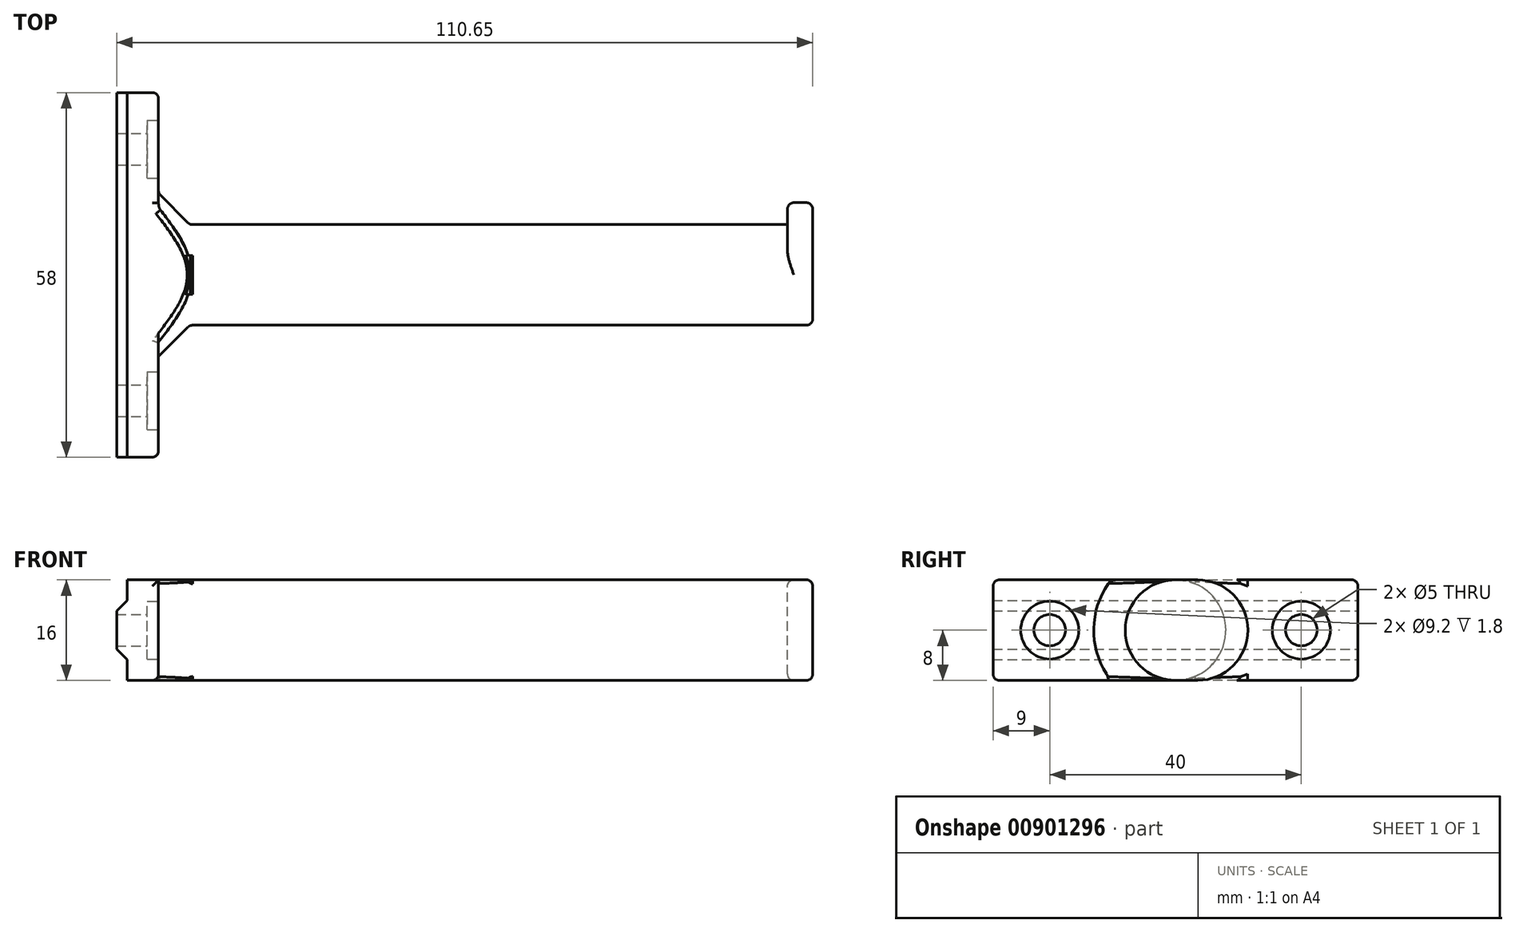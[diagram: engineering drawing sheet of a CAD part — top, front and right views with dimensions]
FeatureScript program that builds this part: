
annotation { "Feature Type Name" : "Feature", "Feature Type Description" : "" }
export const myFeature = defineFeature(function(context is Context, id is Id, definition is map)
    precondition{}
    {
        {
            var Q0;
            Q0=qCreatedBy(makeId("Right.planeOp"),FACE);
            var sketch = newSketch(context, id + "F0", { "sketchPlane" : qUnion([Q0])});
            skCircle(sketch, "E0", {"center": v(0, 0) * mm, "radius": 8 * mm});
            skSolve(sketch);
        }
        {
            var Q0;
            Q0=qSketchRegion(id+"F0",true);
            extrude(context, id + "F1", {"entities" : qUnion([Q0]), "depth" : 95 * mm});
        }
        {
            var Q0;
            Q0=makeQuery(id+"F1.opExtrude","CAP_FACE",FACE,{"disambiguationData":[OSD([sQuery(id+"F0.wireOp",EDGE,"E0")])],"isStart":false});
            var sketch = newSketch(context, id + "F2", { "sketchPlane" : qUnion([Q0])});
            skArc(sketch, "E1", {"start": v(1.75, 7.8) * mm, "mid": v(-8, 0) * mm, "end": v(1.75, -7.8) * mm});
            skLineSegment(sketch, "E2", {"start": v(0, 0) * mm, "end": v(30.67, 0) * mm, "construction": true});
            skArc(sketch, "E3", {"start": v(3.5, -8) * mm, "mid": v(11.5, 0) * mm, "end": v(3.5, 8) * mm});
            skLineSegment(sketch, "E4", {"start": v(3.5, 8) * mm, "end": v(0, 8) * mm});
            skLineSegment(sketch, "E5", {"start": v(3.5, -8) * mm, "end": v(0, -8) * mm});
            skSolve(sketch);
        }
        {
            var Q0;
            Q0=qSketchRegion(id+"F2",true);
            extrude(context, id + "F3", {"entities" : qUnion([Q0]), "operationType" : NewBodyOperationType.ADD, "depth" : 4 * mm});
        }
        {
            var Q0;
            Q0=qCreatedBy(makeId("Top.planeOp"),FACE);
            var sketch = newSketch(context, id + "F4", { "sketchPlane" : qUnion([Q0])});
            skLineSegment(sketch, "E6", {"start": v(0, 0) * mm, "end": v(0, 8) * mm});
            skLineSegment(sketch, "E7", {"start": v(0, 8) * mm, "end": v(-5, 13) * mm});
            skLineSegment(sketch, "E8", {"start": v(-5, 13) * mm, "end": v(-5, 0) * mm});
            skLineSegment(sketch, "E9", {"start": v(26.22, 0) * mm, "end": v(-29.93, 0) * mm, "construction": true});
            skLineSegment(sketch, "E10", {"start": v(0, 0) * mm, "end": v(-5, 0) * mm});
            skSolve(sketch);
        }
        {
            var Q0;
            Q0=qSketchRegion(id+"F4",true);
            var Q1;
            Q1=sQuery(id+"F4.wireOp",EDGE,"E9");
            revolve(context, id + "F5", {"operationType" : NewBodyOperationType.ADD, "entities" : qUnion([Q0]), "axis" : qUnion([Q1]), "revolveType" : RevolveType.FULL});
        }
        {
            var Q0;
            Q0=makeQuery(id+"F5.opRevolve","SWEPT_FACE",FACE,{"disambiguationData":[OSD([sQuery(id+"F4.wireOp",EDGE,"E8")])]});
            var sketch = newSketch(context, id + "F6", { "sketchPlane" : qUnion([Q0])});
            skLineSegment(sketch, "E11", {"start": v(0, 0) * mm, "end": v(-25.76, 0) * mm, "construction": true});
            skLineSegment(sketch, "E12.bottom", {"start": v(-29, -8) * mm, "end": v(29, -8) * mm});
            skLineSegment(sketch, "E12.top", {"start": v(-29, 8) * mm, "end": v(29, 8) * mm});
            skLineSegment(sketch, "E12.left", {"start": v(-29, -8) * mm, "end": v(-29, 8) * mm});
            skLineSegment(sketch, "E12.right", {"start": v(29, -8) * mm, "end": v(29, 8) * mm});
            skPoint(sketch, "E12.middle", {"position": v(0, 0) * mm});
            skPoint(sketch, "E13", {"position": v(-20, 0) * mm});
            skPoint(sketch, "E14.MirrorP", {"position": v(20, 0) * mm});
            skSolve(sketch);
        }
        {
            var Q0;
            Q0=qSketchRegion(id+"F6",true);
            extrude(context, id + "F7", {"entities" : qUnion([Q0]), "operationType" : NewBodyOperationType.ADD, "depth" : 5 * mm});
        }
        {
            var Q0;
            {var subQ0=sQuery(id+"F6.wireOp",EDGE,"E12.bottom");var subQ1=makeQuery(id+"F5.opRevolve","SWEPT_EDGE",EDGE,{"disambiguationData":[OSD([sQuery(id+"F4.wireOp",EDGE,"E7"),sQuery(id+"F4.wireOp",EDGE,"E8")])]});var subQ2=makeQuery(id+"F6.imprint","INTERSECT",VERTEX,{"disambiguationData":[OD(0.0)],"derivedFrom":[subQ1,subQ0]});Q0=makeQuery(id+"F6.imprint","IMPRINT",FACE,{"disambiguationData":[TD([[makeQuery(id+"F6.imprint","IMPRINT",EDGE,{"disambiguationData":[TD([[subQ2,-1.0]])],"derivedFrom":subQ0}),-1.0]])]});}
            var sketch = newSketch(context, id + "F8", { "sketchPlane" : qUnion([Q0])});
            skLineSegment(sketch, "E15.bottom", {"start": v(-35.92, -15.92) * mm, "end": v(35.92, -15.92) * mm});
            skLineSegment(sketch, "E15.top", {"start": v(-35.92, 15.92) * mm, "end": v(35.92, 15.92) * mm});
            skLineSegment(sketch, "E15.left", {"start": v(-35.92, -15.92) * mm, "end": v(-35.92, 15.92) * mm});
            skLineSegment(sketch, "E15.right", {"start": v(35.92, -15.92) * mm, "end": v(35.92, 15.92) * mm});
            skPoint(sketch, "E15.middle", {"position": v(0, 0) * mm});
            skLineSegment(sketch, "E16.bottom", {"start": v(-29, -8) * mm, "end": v(29, -8) * mm});
            skLineSegment(sketch, "E16.top", {"start": v(-29, 8) * mm, "end": v(29, 8) * mm});
            skLineSegment(sketch, "E16.left", {"start": v(-29, -8) * mm, "end": v(-29, 8) * mm});
            skLineSegment(sketch, "E16.right", {"start": v(29, -8) * mm, "end": v(29, 8) * mm});
            skSolve(sketch);
        }
        {
            var Q0;
            Q0=qSketchRegion(id+"F8",true);
            extrude(context, id + "F9", {"entities" : qUnion([Q0]), "operationType" : NewBodyOperationType.REMOVE, "endBound" : BoundingType.THROUGH_ALL, "oppositeDirection" : true, "depth" : 25 * mm});
        }
        {
            var Q0;
            Q0=makeQuery(id+"F9.boolean.opBoolean","SPLIT",EDGE,{"disambiguationData":[OD(0.0)],"derivedFrom":makeQuery(id+"F5.boolean.opBoolean","MERGE",EDGE,{"derivedFrom":[makeQuery(id+"F1.opExtrude","CAP_EDGE",EDGE,{"disambiguationData":[OSD([sQuery(id+"F0.wireOp",EDGE,"E0")])],"isStart":true}),makeQuery(id+"F5.opRevolve","SWEPT_EDGE",EDGE,{"disambiguationData":[OSD([sQuery(id+"F4.wireOp",EDGE,"E6"),sQuery(id+"F4.wireOp",EDGE,"E7")])]})]})});
            var Q1;
            Q1=makeQuery(id+"F9.boolean.opBoolean","SPLIT",EDGE,{"disambiguationData":[OD(1.0)],"derivedFrom":makeQuery(id+"F5.boolean.opBoolean","MERGE",EDGE,{"derivedFrom":[makeQuery(id+"F1.opExtrude","CAP_EDGE",EDGE,{"disambiguationData":[OSD([sQuery(id+"F0.wireOp",EDGE,"E0")])],"isStart":true}),makeQuery(id+"F5.opRevolve","SWEPT_EDGE",EDGE,{"disambiguationData":[OSD([sQuery(id+"F4.wireOp",EDGE,"E6"),sQuery(id+"F4.wireOp",EDGE,"E7")])]})]})});
            var Q2;
            {var subQ0=sQuery(id+"F4.wireOp",EDGE,"E7");Q2=makeQuery(id+"F7.boolean.opBoolean","SPLIT",EDGE,{"disambiguationData":[topologyDisambiguationEdgeConnected([makeQuery(id+"F5.opRevolve","SWEPT_FACE",FACE,{"disambiguationData":[OSD([subQ0])]}),makeQuery(id+"F7.opExtrude","CAP_FACE",FACE,{"disambiguationData":[OSD([sQuery(id+"F6.wireOp",EDGE,"E12.bottom"),sQuery(id+"F6.wireOp",EDGE,"E12.top"),sQuery(id+"F6.wireOp",EDGE,"E12.left"),sQuery(id+"F6.wireOp",EDGE,"E12.right")])],"isStart":true})]),OD(0.0)],"derivedFrom":makeQuery(id+"F5.opRevolve","SWEPT_EDGE",EDGE,{"disambiguationData":[OSD([subQ0,sQuery(id+"F4.wireOp",EDGE,"E8")])]})});}
            var Q3;
            {var subQ0=sQuery(id+"F4.wireOp",EDGE,"E7");Q3=makeQuery(id+"F7.boolean.opBoolean","SPLIT",EDGE,{"disambiguationData":[topologyDisambiguationEdgeConnected([makeQuery(id+"F5.opRevolve","SWEPT_FACE",FACE,{"disambiguationData":[OSD([subQ0])]}),makeQuery(id+"F7.opExtrude","CAP_FACE",FACE,{"disambiguationData":[OSD([sQuery(id+"F6.wireOp",EDGE,"E12.bottom"),sQuery(id+"F6.wireOp",EDGE,"E12.top"),sQuery(id+"F6.wireOp",EDGE,"E12.left"),sQuery(id+"F6.wireOp",EDGE,"E12.right")])],"isStart":true})]),OD(1.0)],"derivedFrom":makeQuery(id+"F5.opRevolve","SWEPT_EDGE",EDGE,{"disambiguationData":[OSD([subQ0,sQuery(id+"F4.wireOp",EDGE,"E8")])]})});}
            var Q4;
            {var subQ0=sQuery(id+"F6.wireOp",EDGE,"E12.left");var subQ1=sQuery(id+"F6.wireOp",EDGE,"E12.top");var subQ2=makeQuery(id+"F7.opExtrude","CAP_FACE",FACE,{"disambiguationData":[OSD([sQuery(id+"F6.wireOp",EDGE,"E12.bottom"),subQ1,subQ0,sQuery(id+"F6.wireOp",EDGE,"E12.right")])],"isStart":true});var subQ3=makeQuery(id+"F7.opExtrude","SWEPT_FACE",FACE,{"disambiguationData":[OSD([subQ1])]});Q4=makeQuery(id+"F7.boolean.opBoolean","SPLIT",EDGE,{"disambiguationData":[topologyDisambiguationEdgeConnected([subQ2,subQ3]),TD([makeQuery(id+"F7.opExtrude","SWEPT_FACE",FACE,{"disambiguationData":[OSD([subQ0])]})])],"derivedFrom":makeQuery(id+"F7.opExtrude","CAP_EDGE",EDGE,{"disambiguationData":[OSD([subQ1])],"isStart":true})});}
            var Q5;
            Q5=makeQuery(id+"F7.opExtrude","CAP_EDGE",EDGE,{"disambiguationData":[OSD([sQuery(id+"F6.wireOp",EDGE,"E12.left")])],"isStart":true});
            var Q6;
            {var subQ0=sQuery(id+"F6.wireOp",EDGE,"E12.left");var subQ1=sQuery(id+"F6.wireOp",EDGE,"E12.bottom");var subQ2=makeQuery(id+"F7.opExtrude","CAP_FACE",FACE,{"disambiguationData":[OSD([subQ1,sQuery(id+"F6.wireOp",EDGE,"E12.top"),subQ0,sQuery(id+"F6.wireOp",EDGE,"E12.right")])],"isStart":true});var subQ3=makeQuery(id+"F7.opExtrude","SWEPT_FACE",FACE,{"disambiguationData":[OSD([subQ1])]});Q6=makeQuery(id+"F7.boolean.opBoolean","SPLIT",EDGE,{"disambiguationData":[topologyDisambiguationEdgeConnected([subQ3,subQ2]),TD([makeQuery(id+"F7.opExtrude","SWEPT_FACE",FACE,{"disambiguationData":[OSD([subQ0])]})])],"derivedFrom":makeQuery(id+"F7.opExtrude","CAP_EDGE",EDGE,{"disambiguationData":[OSD([subQ1])],"isStart":true})});}
            var Q7;
            Q7=makeQuery(id+"F9.boolean.opBoolean","INTERSECT",EDGE,{"disambiguationData":[OD(0.0)],"derivedFrom":[makeQuery(id+"F5.opRevolve","SWEPT_FACE",FACE,{"disambiguationData":[OSD([sQuery(id+"F4.wireOp",EDGE,"E7")])]}),makeQuery(id+"F9.opExtrude","SWEPT_FACE",FACE,{"disambiguationData":[OSD([sQuery(id+"F8.wireOp",EDGE,"E16.bottom")])]})]});
            var Q8;
            Q8=makeQuery(id+"F9.boolean.opBoolean","INTERSECT",EDGE,{"disambiguationData":[OD(1.0)],"derivedFrom":[makeQuery(id+"F5.opRevolve","SWEPT_FACE",FACE,{"disambiguationData":[OSD([sQuery(id+"F4.wireOp",EDGE,"E7")])]}),makeQuery(id+"F9.opExtrude","SWEPT_FACE",FACE,{"disambiguationData":[OSD([sQuery(id+"F8.wireOp",EDGE,"E16.bottom")])]})]});
            var Q9;
            Q9=makeQuery(id+"F9.boolean.opBoolean","INTERSECT",EDGE,{"disambiguationData":[OD(1.0)],"derivedFrom":[makeQuery(id+"F5.opRevolve","SWEPT_FACE",FACE,{"disambiguationData":[OSD([sQuery(id+"F4.wireOp",EDGE,"E7")])]}),makeQuery(id+"F9.opExtrude","SWEPT_FACE",FACE,{"disambiguationData":[OSD([sQuery(id+"F8.wireOp",EDGE,"E16.top")])]})]});
            var Q10;
            Q10=makeQuery(id+"F7.opExtrude","CAP_EDGE",EDGE,{"disambiguationData":[OSD([sQuery(id+"F6.wireOp",EDGE,"E12.right")])],"isStart":true});
            var Q11;
            Q11=makeQuery(id+"F7.opExtrude","SWEPT_EDGE",EDGE,{"disambiguationData":[OSD([sQuery(id+"F6.wireOp",EDGE,"E12.top"),sQuery(id+"F6.wireOp",EDGE,"E12.left")])]});
            var Q12;
            Q12=makeQuery(id+"F7.opExtrude","SWEPT_EDGE",EDGE,{"disambiguationData":[OSD([sQuery(id+"F6.wireOp",EDGE,"E12.bottom"),sQuery(id+"F6.wireOp",EDGE,"E12.left")])]});
            var Q13;
            Q13=makeQuery(id+"F7.opExtrude","SWEPT_EDGE",EDGE,{"disambiguationData":[OSD([sQuery(id+"F6.wireOp",EDGE,"E12.top"),sQuery(id+"F6.wireOp",EDGE,"E12.right")])]});
            var Q14;
            Q14=makeQuery(id+"F7.opExtrude","SWEPT_EDGE",EDGE,{"disambiguationData":[OSD([sQuery(id+"F6.wireOp",EDGE,"E12.bottom"),sQuery(id+"F6.wireOp",EDGE,"E12.right")])]});
            fillet(context, id + "F10", {"entities" : qUnion([Q0, Q1, Q2, Q3, Q4, Q5, Q6, Q7, Q8, Q9, Q10, Q11, Q12, Q13, Q14]), "radius" : 1 * mm, "tangentPropagation" : true, "allowEdgeOverflow" : false});
        }
        {
            var Q0;
            Q0=makeQuery(id+"F3.opExtrude","CAP_EDGE",EDGE,{"disambiguationData":[OSD([sQuery(id+"F2.wireOp",EDGE,"E3")])],"isStart":true});
            var Q1;
            Q1=makeQuery(id+"F3.opExtrude","CAP_EDGE",EDGE,{"disambiguationData":[OSD([sQuery(id+"F2.wireOp",EDGE,"E3")])],"isStart":false});
            var Q2;
            Q2=makeQuery(id+"F1.opExtrude","CAP_EDGE",EDGE,{"disambiguationData":[OSD([sQuery(id+"F0.wireOp",EDGE,"E0")])],"isStart":false});
            fillet(context, id + "F11", {"entities" : qUnion([Q0, Q1, Q2]), "radius" : 1 * mm, "tangentPropagation" : true, "allowEdgeOverflow" : false});
        }
        {
            var Q0;
            Q0=qCreatedBy(makeId("Front.planeOp"),FACE);
            var sketch = newSketch(context, id + "F12", { "sketchPlane" : qUnion([Q0])});
            skLineSegment(sketch, "E17", {"start": v(-11.65, 3.05) * mm, "end": v(-11.65, -3.05) * mm});
            skLineSegment(sketch, "E18", {"start": v(-11.65, -3.05) * mm, "end": v(-10, -4.7) * mm});
            skLineSegment(sketch, "E19", {"start": v(-10, -4.7) * mm, "end": v(-10, 4.7) * mm});
            skLineSegment(sketch, "E20", {"start": v(-10, 4.7) * mm, "end": v(-11.65, 3.05) * mm});
            skSolve(sketch);
        }
        {
            var Q0;
            Q0=qSketchRegion(id+"F12",true);
            var Q1;
            Q1=makeQuery(id+"F7.opExtrude","SWEPT_FACE",FACE,{"disambiguationData":[OSD([sQuery(id+"F6.wireOp",EDGE,"E12.right")])]});
            var Q2;
            Q2=makeQuery(id+"F7.opExtrude","SWEPT_FACE",FACE,{"disambiguationData":[OSD([sQuery(id+"F6.wireOp",EDGE,"E12.left")])]});
            extrude(context, id + "F13", {"entities" : qUnion([Q0]), "operationType" : NewBodyOperationType.ADD, "endBound" : BoundingType.UP_TO_SURFACE, "endBoundEntityFace" : qUnion([Q1]), "depth" : 25 * mm, "hasSecondDirection" : true, "secondDirectionBound" : SecondDirectionBoundingType.UP_TO_SURFACE, "secondDirectionOppositeDirection" : true, "secondDirectionBoundEntityFace" : qUnion([Q2]), "secondDirectionDepth" : 25 * mm});
        }
        {
            var Q0;
            Q0=sQuery(id+"F6.wireOp",VERTEX,"E13");
            var Q1;
            Q1=sQuery(id+"F6.wireOp",VERTEX,"E14.MirrorP");
            var Q2;
            Q2=makeQuery(id+"F1.opExtrude","SWEPT_BODY",BODY,{"disambiguationData":[OSD([sQuery(id+"F0.wireOp",EDGE,"E0")])]});
            hole(context, id + "F14", {"style" : HoleStyle.C_BORE, "endStyle" : HoleEndStyle.BLIND, "oppositeDirection" : true, "holeDiameter" : 5 * mm, "cBoreDiameter" : 9.2 * mm, "cBoreDepth" : 1.8 * mm, "holeDepth" : 12 * mm, "isTappedThrough" : true, "tappedDepth" : 12 * mm, "tapClearance" : 3, "locations" : qUnion([Q0, Q1]), "scope" : qUnion([Q2])});
        }
    });
